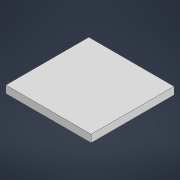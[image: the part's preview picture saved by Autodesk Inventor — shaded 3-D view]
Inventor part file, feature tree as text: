
AUTODESK INVENTOR PART (.ipt)
format: ipt  version: 2022 (Build 260153000, 153)  size: 84,992 bytes
history: native  units: mm
features: other x1, extrude x1, sketch x1
ambient origin geometry x8: Origin, YZ Plane, XZ Plane, XY Plane, X Axis, Y Axis, Z Axis, Center Point
bodies: Body1 (feature_tree)
feature tree (3):
  other  "Твердое тело1"
  extrude  "Выдавливание1"  Depth=253.0mm
  sketch  "Эскиз1"
